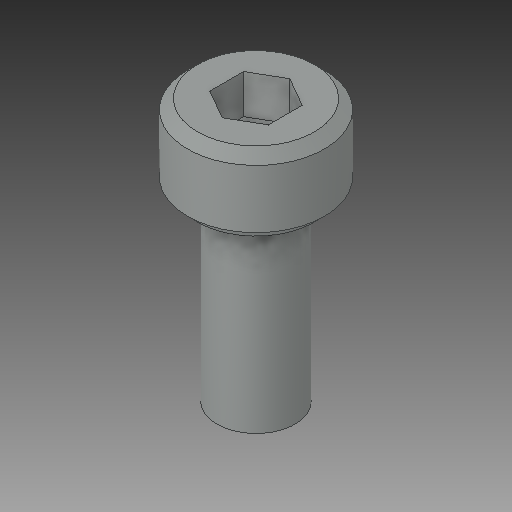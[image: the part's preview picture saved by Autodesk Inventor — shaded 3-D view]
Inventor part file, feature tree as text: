
AUTODESK INVENTOR PART (.ipt)
format: ipt  version: 2017 (Build 210142000, 142)  size: 108,544 bytes
history: native  units: in
note: dims shown in document units (in); Inventor stores cm internally (conversion verified against a paired STEP export)
features: chamfer x1
ambient origin geometry x8: Origin, YZ Plane, XZ Plane, XY Plane, X Axis, Y Axis, Z Axis, Center Point
bodies: Solid1 (feature_tree)
feature tree (1):
  chamfer  "Chamfer2"  [1 undecoded]
note: 1 required parameter value undecoded (feature->parameter linkage not recoverable at this tier; creation-order binding heuristic only, values carry confidence <= 0.55)
